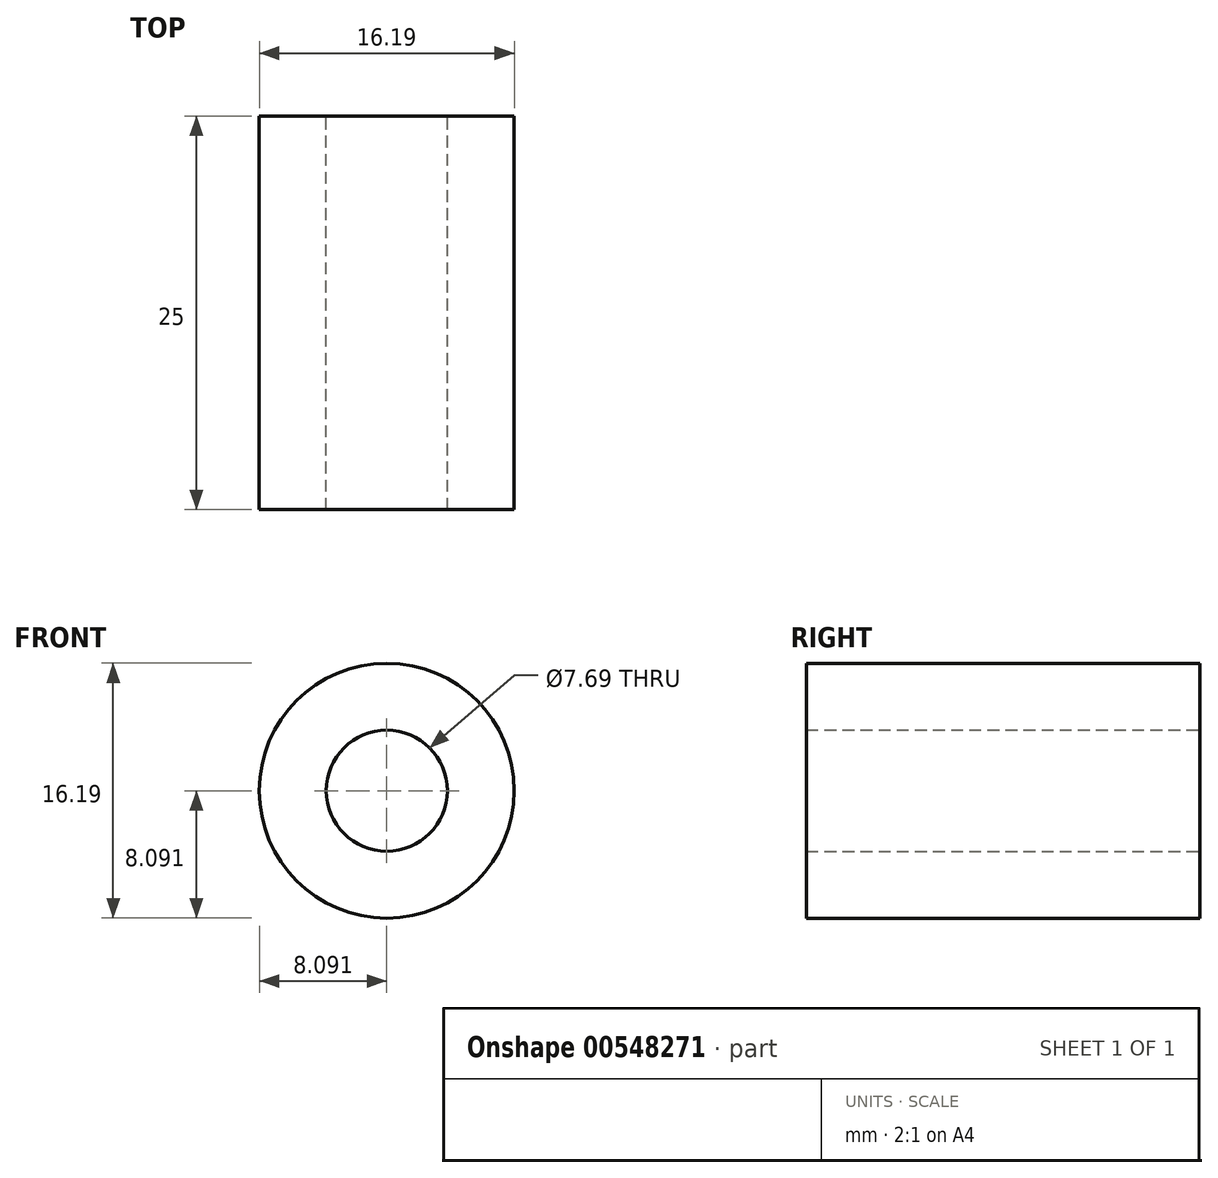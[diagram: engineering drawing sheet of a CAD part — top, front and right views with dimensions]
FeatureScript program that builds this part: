
annotation { "Feature Type Name" : "Feature", "Feature Type Description" : "" }
export const myFeature = defineFeature(function(context is Context, id is Id, definition is map)
    precondition{}
    {
        {
            var Q0;
            Q0=qCreatedBy(makeId("Front.planeOp"),FACE);
            var sketch = newSketch(context, id + "F0", { "sketchPlane" : qUnion([Q0])});
            skCircle(sketch, "E0", {"center": v(74.95, -6.72) * mm, "radius": 3.84 * mm});
            skCircle(sketch, "E1", {"center": v(74.95, -6.72) * mm, "radius": 8.1 * mm});
            skSolve(sketch);
        }
        {
            var Q0;
            Q0=qSketchRegion(id+"F0",true);
            extrude(context, id + "F1", {"entities" : qUnion([Q0]), "depth" : 25 * mm});
        }
    });
